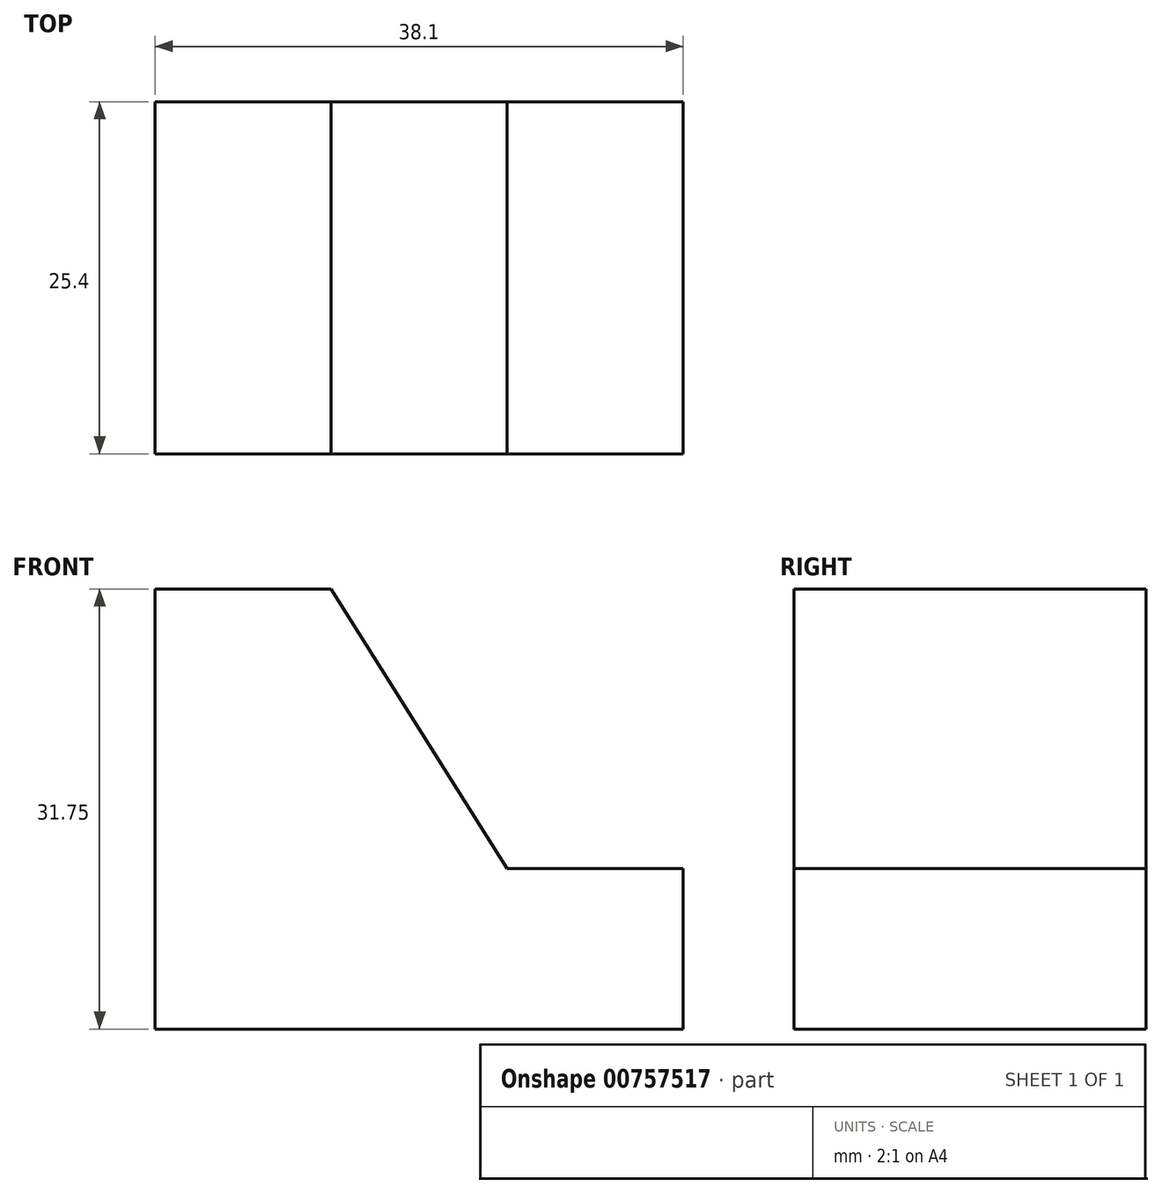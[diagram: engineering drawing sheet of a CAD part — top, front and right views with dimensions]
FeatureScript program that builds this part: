
annotation { "Feature Type Name" : "Feature", "Feature Type Description" : "" }
export const myFeature = defineFeature(function(context is Context, id is Id, definition is map)
    precondition{}
    {
        {
            var Q0;
            Q0=qCreatedBy(makeId("Front.planeOp"),FACE);
            var sketch = newSketch(context, id + "F0", { "sketchPlane" : qUnion([Q0])});
            skLineSegment(sketch, "E0", {"start": v(0, 0) * mm, "end": v(0, 31.75) * mm});
            skLineSegment(sketch, "E1", {"start": v(0, 31.75) * mm, "end": v(-38.1, 31.75) * mm});
            skLineSegment(sketch, "E2", {"start": v(-38.1, 31.75) * mm, "end": v(-38.1, 0) * mm});
            skLineSegment(sketch, "E3", {"start": v(-38.1, 0) * mm, "end": v(0, 0) * mm});
            skSolve(sketch);
        }
        {
            var Q0;
            Q0 = qSketchRegion(id + "F0", true);
            extrude(context, id + "F1", {"entities" : qUnion([Q0]), "depth" : 25.4 * mm, "offsetDistance" : 25.4 * mm});
        }
        {
            var Q0;
            Q0=makeQuery(id+"F1.opExtrude","CAP_FACE",FACE,{"disambiguationData":[OSD([sQuery(id+"F0.wireOp",EDGE,"E0"),sQuery(id+"F0.wireOp",EDGE,"E1"),sQuery(id+"F0.wireOp",EDGE,"E2"),sQuery(id+"F0.wireOp",EDGE,"E3")])],"isStart":true});
            var sketch = newSketch(context, id + "F2", { "sketchPlane" : qUnion([Q0])});
            skLineSegment(sketch, "E4", {"start": v(0, 11.59) * mm, "end": v(12.7, 11.59) * mm});
            skLineSegment(sketch, "E5", {"start": v(12.7, 11.59) * mm, "end": v(25.4, 31.75) * mm});
            skSolve(sketch);
        }
        {
            var Q0;
            {var subQ0=sQuery(id+"F2.wireOp",EDGE,"E4");Q0=makeQuery(id+"F2.imprint","IMPRINT",FACE,{"disambiguationData":[TD([[makeQuery(id+"F2.imprint","IMPRINT",EDGE,{"derivedFrom":subQ0}),1.0]])]});}
            extrude(context, id + "F3", {"entities" : qUnion([Q0]), "operationType" : NewBodyOperationType.REMOVE, "endBound" : BoundingType.THROUGH_ALL, "oppositeDirection" : true, "depth" : 25.4 * mm, "offsetDistance" : 25.4 * mm});
        }
    });
